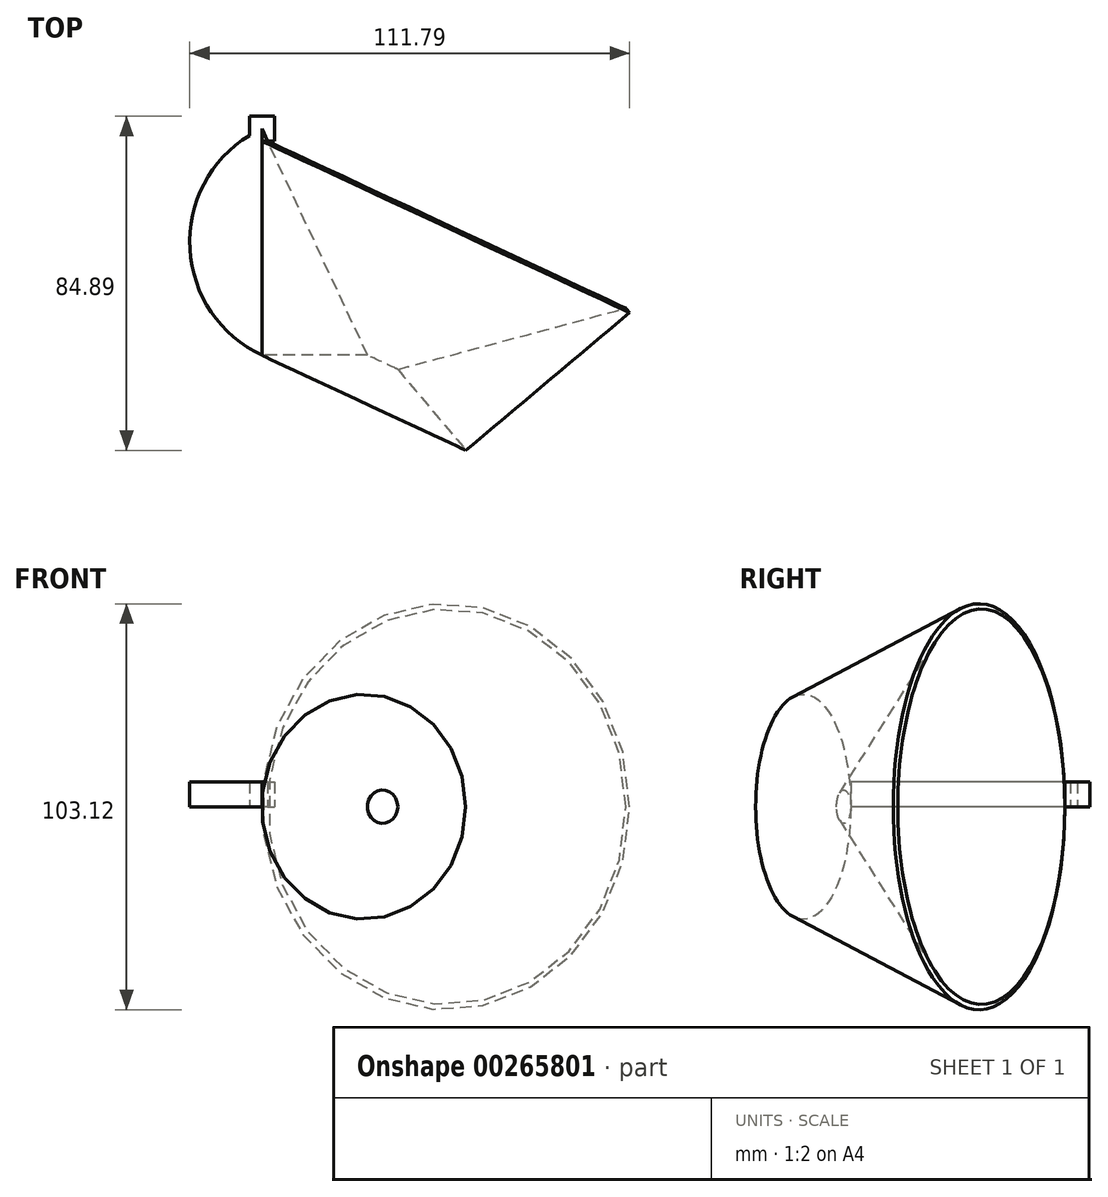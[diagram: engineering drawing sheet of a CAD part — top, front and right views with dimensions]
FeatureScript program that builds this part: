
annotation { "Feature Type Name" : "Feature", "Feature Type Description" : "" }
export const myFeature = defineFeature(function(context is Context, id is Id, definition is map)
    precondition{}
    {
        {
            var Q0;
            Q0=qCreatedBy(makeId("Top.planeOp"),FACE);
            var sketch = newSketch(context, id + "F0", { "sketchPlane" : qUnion([Q0])});
            skLineSegment(sketch, "E0", {"start": v(0, 0) * mm, "end": v(-26.84, 57.55) * mm});
            skArc(sketch, "E1", {"start": v(-26.84, 57.55) * mm, "mid": v(-45.17, 28.78) * mm, "end": v(-26.84, 0) * mm});
            skLineSegment(sketch, "E2", {"start": v(-26.84, 0) * mm, "end": v(0, 0) * mm});
            skLineSegment(sketch, "E3", {"start": v(-26.84, 57.55) * mm, "end": v(-26.84, 0) * mm});
            skLineSegment(sketch, "E4", {"start": v(0, -10.07) * mm, "end": v(42.72, 81.53) * mm});
            skPoint(sketch, "E5", {"position": v(-26.84, 57.55) * mm});
            skLineSegment(sketch, "E6.bottom", {"start": v(-30.01, 54.38) * mm, "end": v(-23.66, 54.38) * mm});
            skLineSegment(sketch, "E6.top", {"start": v(-30.01, 60.73) * mm, "end": v(-23.66, 60.73) * mm});
            skLineSegment(sketch, "E6.left", {"start": v(-30.01, 54.38) * mm, "end": v(-30.01, 60.73) * mm});
            skLineSegment(sketch, "E6.right", {"start": v(-23.66, 54.38) * mm, "end": v(-23.66, 60.73) * mm});
            skSolve(sketch);
        }
        {
            var Q0;
            {var subQ3=sQuery(id+"F0.wireOp",EDGE,"E6.left");var subQ5=sQuery(id+"F0.wireOp",EDGE,"E6.bottom");var subQ7=makeQuery(id+"F0.imprint","INTERSECT",VERTEX,{"derivedFrom":[subQ5,subQ3]});Q0=makeQuery(id+"F0.imprint","IMPRINT",FACE,{"disambiguationData":[TD([[makeQuery(id+"F0.imprint","IMPRINT",EDGE,{"disambiguationData":[TD([[subQ7,-1.0]])],"derivedFrom":subQ5}),-1.0]])]});}
            var Q1;
            {var subQ3=sQuery(id+"F0.wireOp",EDGE,"E6.left");var subQ5=sQuery(id+"F0.wireOp",EDGE,"E6.bottom");var subQ7=makeQuery(id+"F0.imprint","INTERSECT",VERTEX,{"derivedFrom":[subQ5,subQ3]});Q1=makeQuery(id+"F0.imprint","IMPRINT",FACE,{"disambiguationData":[TD([[makeQuery(id+"F0.imprint","IMPRINT",EDGE,{"disambiguationData":[TD([[subQ7,-1.0]])],"derivedFrom":subQ5}),1.0]])]});}
            var Q2;
            {var subQ0=sQuery(id+"F0.wireOp",EDGE,"E6.top");Q2=makeQuery(id+"F0.imprint","IMPRINT",FACE,{"disambiguationData":[TD([[makeQuery(id+"F0.imprint","IMPRINT",EDGE,{"derivedFrom":subQ0}),-1.0]])]});}
            extrude(context, id + "F1", {"entities" : qUnion([Q0, Q1, Q2]), "depth" : 6.35 * mm});
        }
        {
            var Q0;
            {var subQ0=sQuery(id+"F0.wireOp",EDGE,"E2");Q0=makeQuery(id+"F0.imprint","IMPRINT",FACE,{"disambiguationData":[TD([[makeQuery(id+"F0.imprint","IMPRINT",EDGE,{"derivedFrom":subQ0}),1.0]])]});}
            var Q1;
            Q1=sQuery(id+"F0.wireOp",EDGE,"E4");
            revolve(context, id + "F2", {"entities" : qUnion([Q0]), "axis" : qUnion([Q1]), "revolveType" : RevolveType.FULL});
        }
    });
